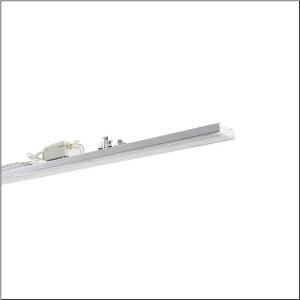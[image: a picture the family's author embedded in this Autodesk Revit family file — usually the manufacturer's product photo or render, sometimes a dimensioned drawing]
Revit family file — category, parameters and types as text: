
# Revit family: licross_11_recessed_mo_51te14mn49xg
name_source: partatom
category: Lighting Fixtures
units: mm (PartAtom-declared; Revit-internal decimal feet)

## family parameters
Cut with Voids When Loaded = No
Host = Face
Light Source = No
Part Type = Normal
Room Calculation Point = No
Round Connector Dimension = Use Diameter
Shared = No

## types (1)
- --- (1 x LED, 9470 lm, 55.2 W, 4000K)
    Apparent Load = 55 VA
    CIE Flux Codes = 56 84 97 100 100
    Color Rendering = 80
    Color Temperature = 4000K
    Default Elevation = 1800 mm
    Description = Licross 11 Recessed MO, luminaire insert, of sheet steel, galvanised, coil coated, white, length: 1.500mm, width: 66mm, height: 67mm, LED rated luminous flux: 9.470lm, light colour: 840, SDCM (Standard Deviation of Colour Matching)MacAdam ≤ 2 SDCM (initial), control gear: ON/OFF Multilumen, with plug, 3-pole, with phase selection, mains connection: 220..240V, AC, 50/60Hz, rated input power: 55W, internal wiring halogen-free, primary light control with lens, of plastic, primary optical cover: cover, of PMMA, light emission: direct distribution, primary light characteristic: asymmetric, protection rating (complete): IP54, insulation class (complete): insulation class I (protective earthing), certification: CE, ENEC, VDE, UKCA, protection symbol: D if used in an environment with non-conductive dust loads with corresponding accessories, impact resistance: IK06, permissible ambient temperature for indoor applications: -35..+40°C, corresponds to IFS (International Featured Standards) requirements for safety and quality in the food industry, reducing of maximum allowable ambient temperature of 5°C with ceiling mounting, The light source and the operating device comply with the requirements of the Ecodesign Regulation (EU) 2019/2020 and are replaceable in accordance with this regulation, packaging unit: 1 piece
    Height = 58 mm
    Lamp = 1 x LED
    Lamp Light Flux = 9470 lm
    Lamp Power = 55.2 W
    Lamp count = 1
    Length = 1500 mm
    Luminous efficacy = 172 lm/W
    Manufacturer = Siteco
    ModVariant = No
    Model = 51TE14MN49XG
    Mounting Place = Ceiling
    Mounting Type = Pendant
    Number of Poles = 1
    OnlyDefault = Yes
    Power Factor = 1
    Product Name = Licross 11 Recessed MO
    Product group = luminaire insert | ceiling pendant
    ProductGroupID = 901
    Protection Class = Protection class I
    Protection Degree = IP 54
    RLX_Detail_Level = 1
    RLX_Emergency_Light_Flux = 0 lm
    RLX_Emergency_Type = 0
    RLX_Emergency_Type_DB = No
    RlxData = <blob elided: 22969 chars, md5=0be56850>
    Socket = socket
    Standby Power = 0 W
    System Light Flux = 9470 lm
    System Power = 55 W
    Type Comments = factory setting: luminous flux: 100 % | (A | C | E) | 126 mA
    Type Image = l_1296930.jpg
    URL = http://relux.com
    VarID = @adj_091537
    Voltage = 0 V
    Weight = 0.00 kg
    Width = 66 mm

## geometry (parser evidence)
native form markers: Blend x4, Sweep x11
no freeform markers — native parametric forms only
